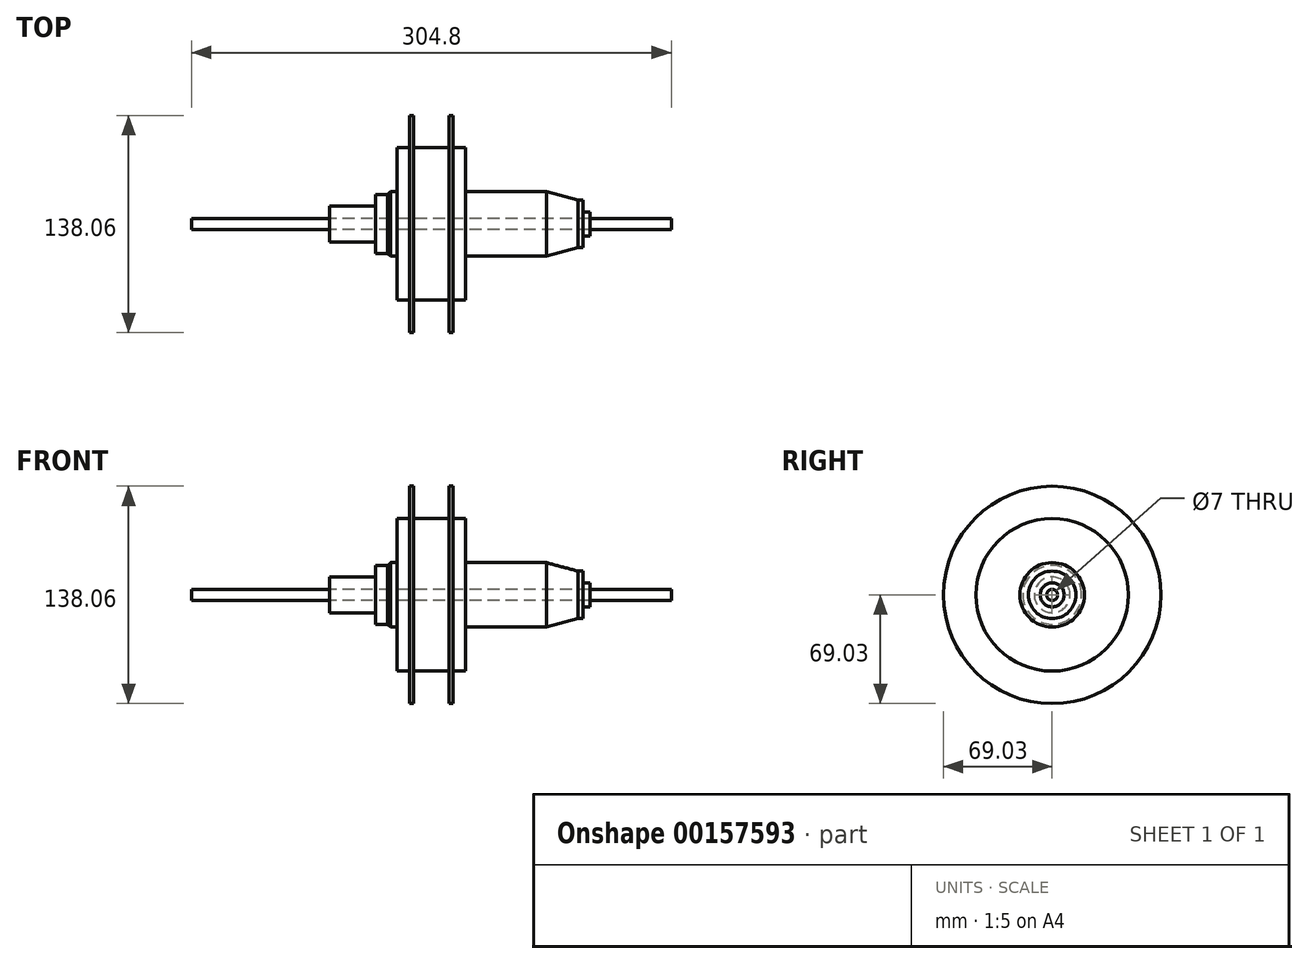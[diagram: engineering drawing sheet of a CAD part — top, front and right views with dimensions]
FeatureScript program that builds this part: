
annotation { "Feature Type Name" : "Feature", "Feature Type Description" : "" }
export const myFeature = defineFeature(function(context is Context, id is Id, definition is map)
    precondition{}
    {
        {
            var Q0;
            Q0=qCreatedBy(makeId("Right.planeOp"),FACE);
            var sketch = newSketch(context, id + "F0", { "sketchPlane" : qUnion([Q0])});
            skCircle(sketch, "E0", {"center": v(0, 0) * mm, "radius": 3.5 * mm});
            skSolve(sketch);
        }
        {
            var Q0;
            Q0 = qSketchRegion(id + "F0", true);
            extrude(context, id + "F1", {"entities" : qUnion([Q0]), "depth" : 304.8 * mm, "symmetric" : true});
        }
        {
            var Q0;
            Q0=qCreatedBy(makeId("Front.planeOp"),FACE);
            var sketch = newSketch(context, id + "F2", { "sketchPlane" : qUnion([Q0])});
            skLineSegment(sketch, "E1", {"start": v(0, 0) * mm, "end": v(176.33, 0) * mm, "construction": true});
            skLineSegment(sketch, "E2", {"start": v(0, 0) * mm, "end": v(0, 89.06) * mm, "construction": true});
            skLineSegment(sketch, "E3", {"start": v(-152.4, 3.5) * mm, "end": v(152.4, 3.5) * mm});
            skLineSegment(sketch, "E4", {"start": v(152.4, -3.5) * mm, "end": v(-152.4, -3.5) * mm});
            skLineSegment(sketch, "E5", {"start": v(-64.83, 3.5) * mm, "end": v(-64.83, 11.36) * mm});
            skLineSegment(sketch, "E6", {"start": v(-64.83, 11.36) * mm, "end": v(-35.34, 11.36) * mm});
            skLineSegment(sketch, "E7", {"start": v(-35.34, 11.36) * mm, "end": v(-35.34, 18.65) * mm});
            skLineSegment(sketch, "E8", {"start": v(-35.34, 18.65) * mm, "end": v(-27.74, 18.65) * mm});
            skLineSegment(sketch, "E9", {"start": v(-27.74, 18.65) * mm, "end": v(-25.84, 20.47) * mm});
            skLineSegment(sketch, "E10", {"start": v(-25.84, 20.47) * mm, "end": v(-21.77, 20.47) * mm});
            skLineSegment(sketch, "E11", {"start": v(-21.77, 20.47) * mm, "end": v(-21.77, 48.4) * mm});
            skLineSegment(sketch, "E12", {"start": v(-21.77, 48.4) * mm, "end": v(-13.83, 48.4) * mm});
            skLineSegment(sketch, "E13", {"start": v(-13.83, 48.4) * mm, "end": v(-13.83, 69.03) * mm});
            skLineSegment(sketch, "E14", {"start": v(-13.83, 69.03) * mm, "end": v(-11.26, 69.03) * mm});
            skLineSegment(sketch, "E15", {"start": v(-11.26, 69.03) * mm, "end": v(-11.26, 48.4) * mm});
            skLineSegment(sketch, "E16", {"start": v(-11.26, 48.4) * mm, "end": v(0, 48.4) * mm});
            skPoint(sketch, "E16.endSnap0", {"position": v(0, 44.53) * mm});
            skLineSegment(sketch, "E17.MirrorCS", {"start": v(11.26, 48.4) * mm, "end": v(0, 48.4) * mm});
            skLineSegment(sketch, "E18.MirrorCS", {"start": v(11.26, 69.03) * mm, "end": v(11.26, 48.4) * mm});
            skLineSegment(sketch, "E19.MirrorCS", {"start": v(13.83, 48.4) * mm, "end": v(13.83, 69.03) * mm});
            skLineSegment(sketch, "E20.MirrorCS", {"start": v(13.83, 69.03) * mm, "end": v(11.26, 69.03) * mm});
            skLineSegment(sketch, "E21.MirrorCS", {"start": v(21.77, 48.4) * mm, "end": v(13.83, 48.4) * mm});
            skLineSegment(sketch, "E22.MirrorCS", {"start": v(21.77, 20.47) * mm, "end": v(21.77, 48.4) * mm});
            skLineSegment(sketch, "E23", {"start": v(21.77, 20.47) * mm, "end": v(73, 20.47) * mm});
            skLineSegment(sketch, "E24", {"start": v(73, 20.47) * mm, "end": v(93.02, 15.08) * mm});
            skLineSegment(sketch, "E25", {"start": v(93.02, 15.08) * mm, "end": v(96.11, 15.08) * mm});
            skLineSegment(sketch, "E26", {"start": v(96.11, 15.08) * mm, "end": v(96.11, 7.62) * mm});
            skLineSegment(sketch, "E27", {"start": v(96.11, 7.62) * mm, "end": v(100.66, 7.62) * mm});
            skLineSegment(sketch, "E28", {"start": v(100.66, 7.62) * mm, "end": v(100.66, 3.5) * mm});
            skSolve(sketch);
        }
        {
            var Q0;
            {var subQ0=sQuery(id+"F2.wireOp",EDGE,"E5");Q0=makeQuery(id+"F2.imprint","IMPRINT",FACE,{"disambiguationData":[TD([[makeQuery(id+"F2.imprint","IMPRINT",EDGE,{"derivedFrom":subQ0}),-1.0]])]});}
            var Q1;
            Q1=sQuery(id+"F2.wireOp",EDGE,"E1");
            revolve(context, id + "F3", {"entities" : qUnion([Q0]), "axis" : qUnion([Q1]), "revolveType" : RevolveType.FULL});
        }
    });
